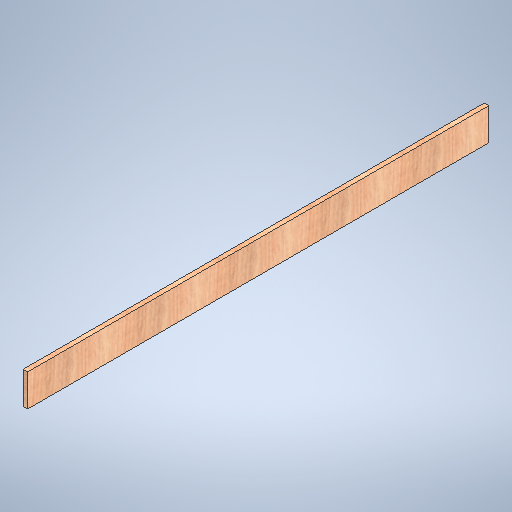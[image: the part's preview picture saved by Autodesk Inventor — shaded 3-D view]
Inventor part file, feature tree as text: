
AUTODESK INVENTOR PART (.ipt)
format: ipt  version: 2025 (Build 290162010, 162A)  size: 310,784 bytes
history: native  units: in
note: dims shown in document units (in); Inventor stores cm internally (conversion verified against a paired STEP export)
features: extrude x1, sketch x1
ambient origin geometry x8: Origin, YZ Plane, XZ Plane, XY Plane, X Axis, Y Axis, Z Axis, Center Point
bodies: Solid1 (feature_tree)
feature tree (2):
  extrude  "Extrusion1"  Depth=0.5in TaperAngle=0.0deg
  sketch  "Sketch1"  dims[d1=50.25in d2=0.5in d3=0.0in d4=3.5in]
